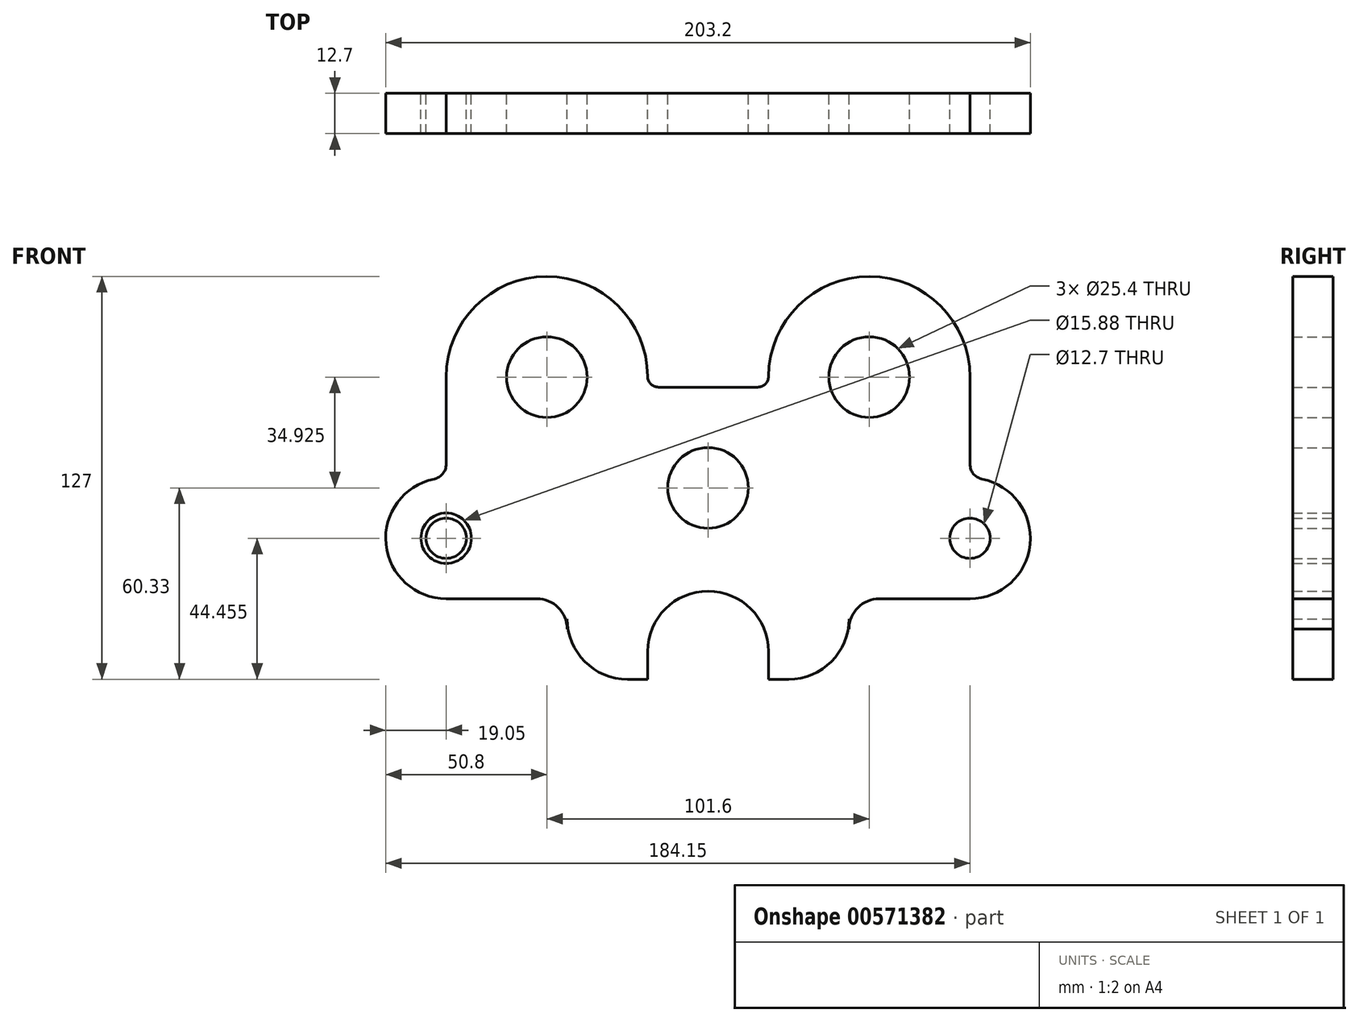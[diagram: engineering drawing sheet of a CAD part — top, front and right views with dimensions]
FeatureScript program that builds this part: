
annotation { "Feature Type Name" : "Feature", "Feature Type Description" : "" }
export const myFeature = defineFeature(function(context is Context, id is Id, definition is map)
    precondition{}
    {
        {
            var Q0;
            Q0=qCreatedBy(makeId("Front.planeOp"),FACE);
            var sketch = newSketch(context, id + "F0", { "sketchPlane" : qUnion([Q0])});
            skArc(sketch, "E0", {"start": v(82.55, 34.93) * mm, "mid": v(50.9, 66.67) * mm, "end": v(19.05, 35.12) * mm});
            skLineSegment(sketch, "E1", {"start": v(82.55, 34.93) * mm, "end": v(82.55, 7.46) * mm});
            skArc(sketch, "E2", {"start": v(82.55, -34.92) * mm, "mid": v(101.5, -17.79) * mm, "end": v(86.36, 2.8) * mm});
            skLineSegment(sketch, "E3", {"start": v(82.55, -34.92) * mm, "end": v(53.98, -34.92) * mm});
            skCircle(sketch, "E4", {"center": v(50.8, 34.93) * mm, "radius": 12.7 * mm});
            skCircle(sketch, "E5", {"center": v(82.55, -15.87) * mm, "radius": 6.35 * mm});
            skLineSegment(sketch, "E6", {"start": v(50.8, 74.41) * mm, "end": v(50.8, -7.1) * mm, "construction": true});
            skPoint(sketch, "E6.startSnap0", {"position": v(50.8, 66.67) * mm});
            skLineSegment(sketch, "E7", {"start": v(72.24, 34.93) * mm, "end": v(7.49, 34.93) * mm, "construction": true});
            skLineSegment(sketch, "E8", {"start": v(82.55, 0) * mm, "end": v(82.55, -56.09) * mm, "construction": true});
            skLineSegment(sketch, "E9", {"start": v(38.27, -15.87) * mm, "end": v(117.37, -15.87) * mm, "construction": true});
            skCircle(sketch, "E10", {"center": v(0, 0) * mm, "radius": 12.7 * mm});
            skLineSegment(sketch, "E11", {"start": v(0, 42.71) * mm, "end": v(0, -64.9) * mm, "construction": true});
            skLineSegment(sketch, "E12", {"start": v(-44.82, 0) * mm, "end": v(29.18, 0) * mm, "construction": true});
            skPoint(sketch, "E13.orphan", {"position": v(0, 34.92) * mm});
            skLineSegment(sketch, "E14", {"start": v(0, 31.75) * mm, "end": v(15.66, 31.75) * mm});
            skLineSegment(sketch, "E15", {"start": v(44.45, -41.27) * mm, "end": v(44.45, -44.45) * mm});
            skLineSegment(sketch, "E16", {"start": v(25.4, -60.32) * mm, "end": v(19.05, -60.32) * mm});
            skLineSegment(sketch, "E17", {"start": v(19.05, -60.32) * mm, "end": v(19.05, -51.59) * mm});
            skPoint(sketch, "E18.visualSharp", {"position": v(19.05, -32.6) * mm});
            skPoint(sketch, "E19.visualSharp", {"position": v(44.45, -60.32) * mm});
            skArc(sketch, "E19.filletArc", {"start": v(25.4, -60.32) * mm, "mid": v(38.87, -54.75) * mm, "end": v(44.45, -41.27) * mm});
            skPoint(sketch, "E20.visualSharp", {"position": v(44.45, -34.92) * mm});
            skArc(sketch, "E20.filletArc", {"start": v(53.98, -34.92) * mm, "mid": v(47.24, -37.71) * mm, "end": v(44.45, -44.45) * mm});
            skPoint(sketch, "E21.visualSharp", {"position": v(82.55, 3.17) * mm});
            skArc(sketch, "E21.filletArc", {"start": v(82.55, 7.46) * mm, "mid": v(83.62, 4.44) * mm, "end": v(86.36, 2.8) * mm});
            skPoint(sketch, "E22.newPointA", {"position": v(19.05, 34.92) * mm});
            skPoint(sketch, "E22.newPointB", {"position": v(7.49, 31.75) * mm});
            skArc(sketch, "E22.filletArc", {"start": v(15.66, 31.75) * mm, "mid": v(18.05, 32.73) * mm, "end": v(19.05, 35.12) * mm});
            skLineSegment(sketch, "E23", {"start": v(-60.5, -47.62) * mm, "end": v(83.9, -47.62) * mm, "construction": true});
            skLineSegment(sketch, "E24.MirrorCS", {"start": v(0, 31.75) * mm, "end": v(-15.66, 31.75) * mm});
            skPoint(sketch, "E25.MirrorP", {"position": v(-7.49, 31.75) * mm});
            skPoint(sketch, "E26.MirrorP", {"position": v(-19.05, 34.92) * mm});
            skArc(sketch, "E27.MirrorCS", {"start": v(-82.55, 34.93) * mm, "mid": v(-50.9, 66.67) * mm, "end": v(-19.05, 35.12) * mm});
            skLineSegment(sketch, "E28.MirrorCS", {"start": v(-82.55, 34.93) * mm, "end": v(-82.55, 7.46) * mm});
            skArc(sketch, "E29.MirrorCS", {"start": v(-82.55, -34.92) * mm, "mid": v(-101.5, -17.79) * mm, "end": v(-86.36, 2.8) * mm});
            skLineSegment(sketch, "E30.MirrorCS", {"start": v(-82.55, -34.93) * mm, "end": v(-53.98, -34.92) * mm});
            skArc(sketch, "E31.MirrorCS", {"start": v(-25.4, -60.32) * mm, "mid": v(-38.87, -54.75) * mm, "end": v(-44.45, -41.27) * mm});
            skLineSegment(sketch, "E32.MirrorCS", {"start": v(-25.4, -60.32) * mm, "end": v(-19.05, -60.32) * mm});
            skLineSegment(sketch, "E33.MirrorCS", {"start": v(-19.05, -60.32) * mm, "end": v(-19.05, -51.59) * mm});
            skPoint(sketch, "E34.newPointA", {"position": v(-86.36, 2.8) * mm});
            skPoint(sketch, "E34.newPointB", {"position": v(-82.55, 7.46) * mm});
            skArc(sketch, "E34.filletArc", {"start": v(-86.36, 2.8) * mm, "mid": v(-83.62, 4.44) * mm, "end": v(-82.55, 7.46) * mm});
            skArc(sketch, "E35.MirrorCS", {"start": v(-53.98, -34.92) * mm, "mid": v(-47.24, -37.71) * mm, "end": v(-44.45, -44.45) * mm});
            skLineSegment(sketch, "E36.MirrorCS", {"start": v(-44.45, -41.27) * mm, "end": v(-44.45, -44.45) * mm});
            skArc(sketch, "E37.MirrorCS", {"start": v(-15.66, 31.75) * mm, "mid": v(-18.05, 32.73) * mm, "end": v(-19.05, 35.12) * mm});
            skCircle(sketch, "E38.MirrorC", {"center": v(-50.8, 34.93) * mm, "radius": 12.7 * mm});
            skCircle(sketch, "E39.MirrorC", {"center": v(-82.55, -15.87) * mm, "radius": 6.35 * mm});
            skArc(sketch, "E40", {"start": v(19.05, -51.59) * mm, "mid": v(0, -32.54) * mm, "end": v(-19.05, -51.59) * mm});
            skLineSegment(sketch, "E41", {"start": v(-101.6, 46.46) * mm, "end": v(-101.6, -66.93) * mm, "construction": true});
            skLineSegment(sketch, "E42", {"start": v(-101.6, -66.93) * mm, "end": v(-101.6, 3.67) * mm, "construction": true});
            skLineSegment(sketch, "E43", {"start": v(-44.45, -4.7) * mm, "end": v(-44.45, -75.32) * mm});
            skLineSegment(sketch, "E44", {"start": v(-17.52, 66.67) * mm, "end": v(-84.96, 66.67) * mm, "construction": true});
            skLineSegment(sketch, "E45", {"start": v(-20.55, -60.32) * mm, "end": v(-66.48, -60.32) * mm, "construction": true});
            skPoint(sketch, "E46.MirrorP", {"position": v(-82.55, 3.17) * mm});
            skArc(sketch, "E47.MirrorCS", {"start": v(-82.55, 7.46) * mm, "mid": v(-83.62, 4.44) * mm, "end": v(-86.36, 2.8) * mm});
            skCircle(sketch, "E48", {"center": v(-82.55, -15.87) * mm, "radius": 7.94 * mm});
            skCircle(sketch, "E49", {"center": v(82.55, -15.87) * mm, "radius": 7.94 * mm});
            skSolve(sketch);
        }
        {
            var Q0;
            Q0=makeQuery(id+"F0.imprint","IMPRINT",FACE,{"disambiguationData":[TD([[makeQuery(id+"F0.imprint","IMPRINT",EDGE,{"derivedFrom":sQuery(id+"F0.wireOp",EDGE,"E0")}),1.0]])]});
            var Q1;
            Q1=makeQuery(id+"F0.imprint","IMPRINT",FACE,{"disambiguationData":[TD([[makeQuery(id+"F0.imprint","IMPRINT",EDGE,{"derivedFrom":sQuery(id+"F0.wireOp",EDGE,"E39.MirrorC")}),1.0]])]});
            var Q2;
            Q2=makeQuery(id+"F0.imprint","IMPRINT",FACE,{"disambiguationData":[TD([[makeQuery(id+"F0.imprint","IMPRINT",EDGE,{"derivedFrom":sQuery(id+"F0.wireOp",EDGE,"E5")}),-1.0]])]});
            extrude(context, id + "F1", {"entities" : qUnion([Q0, Q1, Q2]), "depth" : 12.7 * mm, "offsetDistance" : 25.4 * mm});
        }
    });
